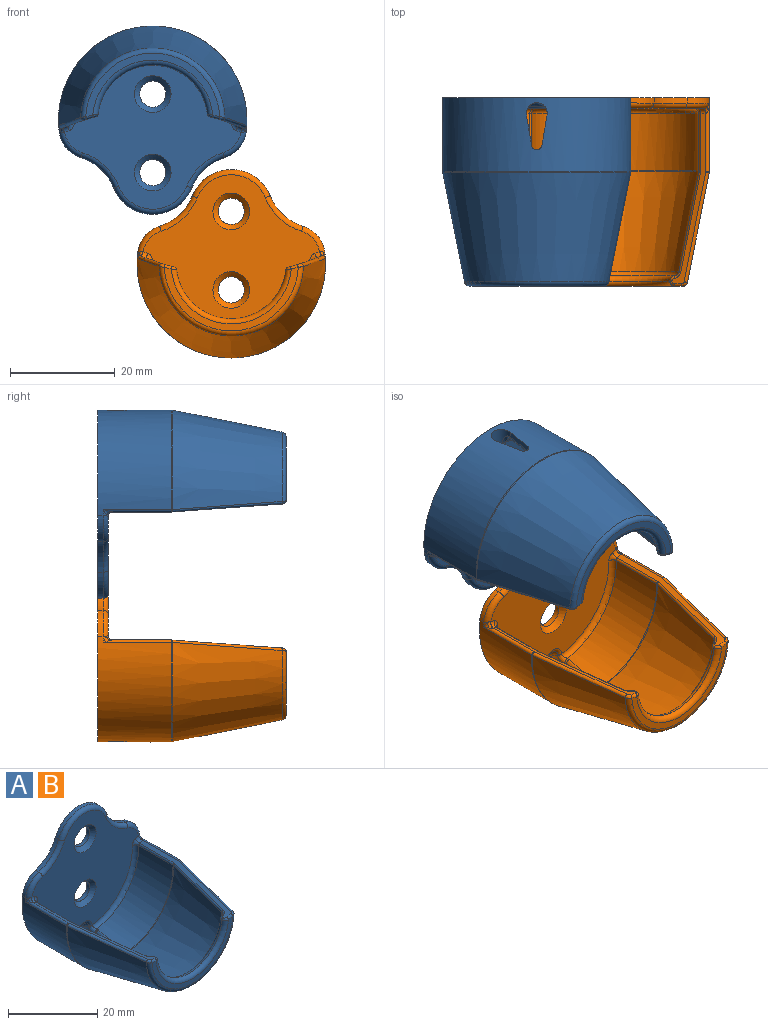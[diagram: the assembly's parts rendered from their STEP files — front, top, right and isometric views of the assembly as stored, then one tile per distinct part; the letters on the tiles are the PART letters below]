
ASSEMBLY  parts=2 mates=1
PART A: 83 faces, bbox 41.4x54.6x38.1 mm
  f0: cylinder r=18mm len=36mm, axis (0,1,0), area 802.1mm2, adj f11,f12,f14,f16,f19,f20,f29,f42
  f1: cylinder r=16mm len=32mm, axis (0,1,0), area 525.8mm2, adj f15,f28,f40,f57,f68,f69,f70,f71
  f2: plane 33.66x31.83mm, normal (0,-1,0), area 618mm2, adj f21,f22,f23,f24,f25,f57,f58,f59
  f3: plane 25.61x12.16mm, normal (0,-1,0), area 48.2mm2, adj f18,f27,f37,f50
  f4: cone r=17.96mm half-angle=11.3deg, axis (0,1,0), area 1071.5mm2, adj f16,f18,f33,f46
  f5: cone r=16mm half-angle=11.3deg, axis (0,1,0), area 856.4mm2, adj f15,f17,f32,f43
  f6: cylinder r=10.5mm len=20.88mm, axis (0,-1,0), area 0.8mm2, adj f26,f27,f38,f49
  f7: cylinder r=45mm len=32.5mm, axis (0,-1,0), area 36mm2, adj f40,f41,f42,f43,f44,f45,f46,f47
  f8: cylinder r=45mm len=32.5mm, axis (0,-1,0), area 36mm2, adj f28,f29,f30,f31,f32,f33,f34,f35
  f9: cylinder r=8mm len=14.85mm, axis (0,-1,0), area 19mm2, adj f10,f13,f14,f25
  f10: cylinder r=10mm len=6.29mm, axis (0,-1,0), area 8.8mm2, adj f9,f11,f14,f24
  f11: cylinder r=6mm len=5.01mm, axis (0,-1,0), area 6.9mm2, adj f0,f10,f14,f22
  f12: cylinder r=6mm len=5.01mm, axis (0,-1,0), area 6.9mm2, adj f0,f13,f14,f21
  f13: cylinder r=10mm len=6.29mm, axis (0,-1,0), area 8.8mm2, adj f9,f12,f14,f23
  f14: plane 36x36mm, normal (0,1,0), area 879.5mm2, adj f0,f9,f10,f11,f12,f13,f79,f80
  f15: torus R=15mm, axis (0,1,0), area 10.1mm2, adj f1,f5,f30,f41
  f16: torus R=17mm, axis (0,-1,0), area 11.6mm2, adj f0,f4,f31,f44
  f17: torus R=11.18mm, axis (0,-1,0), area 43mm2, adj f5,f26,f34,f45
  f18: torus R=12.82mm, axis (0,-1,0), area 56.2mm2, adj f3,f4,f35,f48
  f19: torus R=17mm, axis (0,-1,0), area 0.4mm2, adj f0,f21,f63
  f20: torus R=17mm, axis (0,-1,0), area 0.4mm2, adj f0,f22,f60
  f21: torus R=5mm, axis (0,-1,0), area 9.9mm2, adj f2,f12,f19,f23,f64,f65
  f22: torus R=5mm, axis (0,-1,0), area 9.9mm2, adj f2,f11,f20,f24,f61,f62
  f23: torus R=11mm, axis (0,-1,0), area 14.4mm2, adj f2,f13,f21,f25
  f24: torus R=11mm, axis (0,-1,0), area 14.4mm2, adj f2,f10,f22,f25
  f25: torus R=7mm, axis (0,-1,0), area 28.5mm2, adj f2,f9,f23,f24
  f26: torus R=11.5mm, axis (0,1,0), area 44.8mm2, adj f6,f17,f36,f47
  f27: torus R=11.5mm, axis (0,-1,0), area 50.3mm2, adj f3,f6,f39,f51
  f28: cylinder r=0.5mm len=10.9mm, axis (0,-1,0), area 6.7mm2, adj f1,f8,f30,f58
  f29: cylinder r=0.5mm len=13.1mm, axis (0,1,0), area 11.3mm2, adj f0,f8,f31,f60,f62
  f30: bspline ~0.69x0.53mm, area 0.1mm2, adj f8,f15,f28,f32
  f31: bspline ~0.73x0.72mm, area 0.2mm2, adj f8,f16,f29,f33
  f32: bspline ~50.95x10.43mm, area 12.1mm2, adj f5,f8,f30,f34
  f33: bspline ~44.87x9.42mm, area 20.3mm2, adj f4,f8,f31,f35
  f34: bspline ~1.52x1.41mm, area 1mm2, adj f8,f17,f32,f36
  f35: bspline ~1.38x0.94mm, area 1mm2, adj f8,f18,f33,f37
  f36: bspline ~1.09x1.06mm, area 0.7mm2, adj f8,f26,f34,f38
  f37: torus R=45.5mm, axis (0,-1,0), area 1.1mm2, adj f3,f8,f35,f39
  f38: cylinder r=0.5mm len=0.43mm, axis (0,-1,0), area 0mm2, adj f6,f8,f36,f39
  f39: bspline ~1.25x1.23mm, area 0.9mm2, adj f8,f27,f37,f38
  f40: cylinder r=0.5mm len=10.9mm, axis (0,1,0), area 6.7mm2, adj f1,f7,f41,f67
  f41: bspline ~0.7x0.5mm, area 0.1mm2, adj f7,f15,f40,f43
  f42: cylinder r=0.5mm len=13.1mm, axis (0,-1,0), area 11.3mm2, adj f0,f7,f44,f63,f64
  f43: bspline ~41.67x8.52mm, area 12.1mm2, adj f5,f7,f41,f45
  f44: bspline ~0.76x0.73mm, area 0.2mm2, adj f7,f16,f42,f46
  f45: bspline ~1.64x1.52mm, area 1mm2, adj f7,f17,f43,f47
  f46: bspline ~40.33x8.67mm, area 20.3mm2, adj f4,f7,f44,f48
  f47: bspline ~1.21x0.91mm, area 0.7mm2, adj f7,f26,f45,f49
  f48: bspline ~1.39x1.04mm, area 1mm2, adj f7,f18,f46,f50
  f49: cylinder r=0.5mm len=0.43mm, axis (0,-1,0), area 0mm2, adj f6,f7,f47,f51
  f50: torus R=45.5mm, axis (0,-1,0), area 1.1mm2, adj f3,f7,f48,f51
  f51: bspline ~1.25x1.23mm, area 0.9mm2, adj f7,f27,f49,f50
  f52: plane 5.84x1.24mm, normal (0.99,0.17,0), area 6.6mm2, adj f0,f53,f55,f73
  f53: cylinder r=1mm len=1.97mm, axis (0,0,1), area 3.1mm2, adj f0,f52,f54,f71
  f54: plane 5.84x1.24mm, normal (-0.99,0.17,0), area 6.6mm2, adj f0,f53,f55,f69
  f55: cylinder r=2mm len=4mm, axis (0,0,1), area 15.1mm2, adj f0,f52,f54,f56,f70,f72,f75,f77
  f56: sphere r=2mm, area 4.2mm2, adj f55,f74,f76,f78
  f57: torus R=15mm, axis (0,-1,0), area 35.5mm2, adj f1,f2,f58,f77,f78
  f58: torus R=1.5mm, axis (0,-1,0), area 1.7mm2, adj f2,f28,f57,f59
  f59: torus R=44mm, axis (0,-1,0), area 1.5mm2, adj f2,f8,f58,f61
  f60: bspline ~1.52x1.22mm, area 0.7mm2, adj f20,f29,f62
  f61: bspline ~1.18x1.07mm, area 0.1mm2, adj f8,f22,f59,f62
  f62: bspline ~1.49x1.12mm, area 0.9mm2, adj f22,f29,f60,f61
  f63: bspline ~1.52x1.22mm, area 0.7mm2, adj f19,f42,f64
  f64: bspline ~1.42x1.09mm, area 0.9mm2, adj f21,f42,f63,f65
  f65: bspline ~1.04x1.03mm, area 0.1mm2, adj f7,f21,f64,f66
  f66: torus R=44mm, axis (0,-1,0), area 1.5mm2, adj f2,f7,f65,f67
  f67: torus R=1.5mm, axis (0,-1,0), area 1.7mm2, adj f2,f40,f66,f68
  f68: torus R=15mm, axis (0,-1,0), area 35.5mm2, adj f1,f2,f67,f72,f74
  f69: bspline ~6x1.8mm, area 8.5mm2, adj f1,f54,f70,f71
  f70: bspline ~1.33x1mm, area 0.6mm2, adj f1,f55,f69,f72
  f71: bspline ~3.76x2.12mm, area 5.7mm2, adj f1,f53,f69,f73
  f72: bspline ~2.13x1.41mm, area 2.1mm2, adj f55,f68,f70,f74
  f73: bspline ~6x1.8mm, area 8.5mm2, adj f1,f52,f71,f75
  f74: bspline ~0.75x0.44mm, area 0.1mm2, adj f56,f68,f72,f76
  f75: bspline ~1.81x1.02mm, area 0.6mm2, adj f1,f55,f73,f77
  f76: torus R=2.24mm, axis (0,-1,0), area 4.6mm2, adj f2,f56,f74,f78
  f77: bspline ~2.13x1.61mm, area 2.1mm2, adj f55,f57,f75,f78
  f78: bspline ~0.76x0.4mm, area 0.1mm2, adj f56,f57,f76,f77
  f79: cylinder r=2.5mm len=5mm, axis (0,1,0), area 15.7mm2, adj f14,f81
  f80: cylinder r=2.5mm len=5mm, axis (0,1,0), area 15.7mm2, adj f14,f82
  f81: cone r=2.5mm half-angle=45deg, axis (0,-1,0), area 26.7mm2, adj f2,f79
  f82: cone r=2.5mm half-angle=45deg, axis (0,-1,0), area 26.7mm2, adj f2,f80
PART B: same geometry as A
PLACE A rot(axis=(0,1,0),180deg) t=(-18.57,11.78,-7.11)mm
PLACE B t=(-3.57,11.78,-34.53)mm
MATE fastened A.f2 <-> B.f2  axis (0,-1,0) through (-31.98,11.78,-13.32)mm
